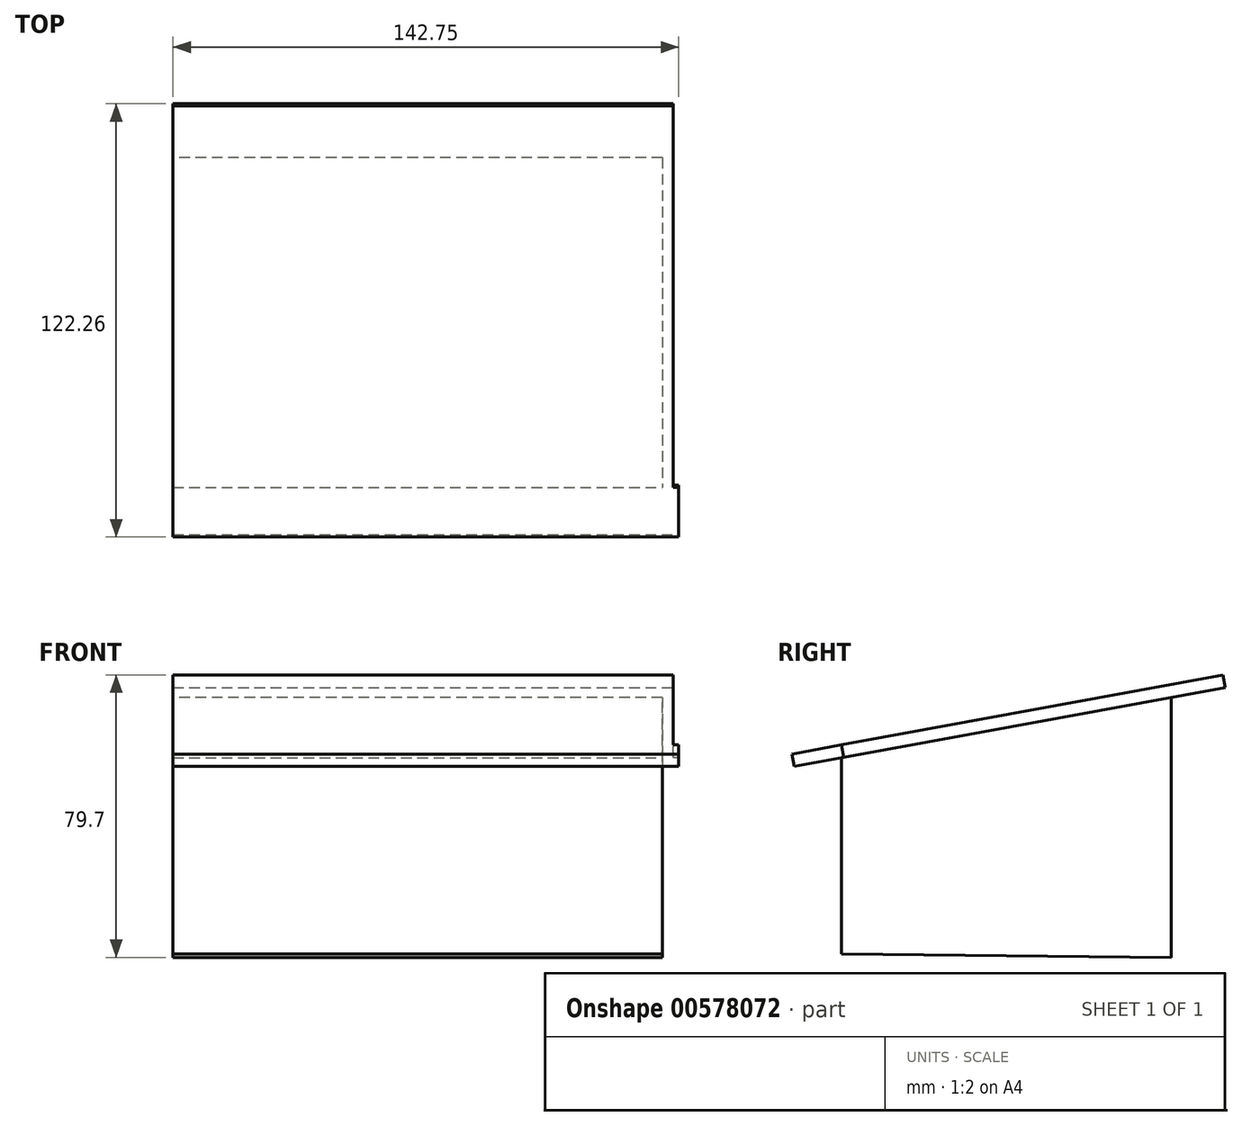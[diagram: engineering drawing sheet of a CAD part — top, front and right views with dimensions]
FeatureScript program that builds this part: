
annotation { "Feature Type Name" : "Feature", "Feature Type Description" : "" }
export const myFeature = defineFeature(function(context is Context, id is Id, definition is map)
    precondition{}
    {
        {
            var Q0;
            Q0=qCreatedBy(makeId("Right.planeOp"),FACE);
            var sketch = newSketch(context, id + "F0", { "sketchPlane" : qUnion([Q0])});
            skLineSegment(sketch, "E0", {"start": v(-41.54, 55.43) * mm, "end": v(-41.54, -3.51) * mm});
            skLineSegment(sketch, "E1", {"start": v(51.47, -4.53) * mm, "end": v(-41.54, -3.51) * mm});
            skLineSegment(sketch, "E2", {"start": v(66.08, 75.17) * mm, "end": v(-41.54, 55.43) * mm});
            skLineSegment(sketch, "E3", {"start": v(-41.54, 55.43) * mm, "end": v(-55.54, 52.86) * mm});
            skLineSegment(sketch, "E4", {"start": v(51.47, -4.53) * mm, "end": v(51.47, 72.5) * mm});
            skSolve(sketch);
        }
        {
            var Q0;
            Q0 = qSketchRegion(id + "F0", true);
            extrude(context, id + "F1", {"entities" : qUnion([Q0]), "depth" : 138.18 * mm, "offsetDistance" : 25.4 * mm});
        }
        {
            var Q0;
            Q0=sQuery(id+"F0.wireOp",EDGE,"E3");
            extrude(context, id + "F2", {"bodyType" : ToolBodyType.SURFACE, "surfaceEntities" : qUnion([Q0]), "depth" : 142.75 * mm, "offsetDistance" : 25.4 * mm});
        }
        {
            var Q0;
            Q0=makeQuery(id+"F2.opExtrude","SWEPT_FACE",FACE,{"disambiguationData":[OSD([sQuery(id+"F0.wireOp",EDGE,"E3")])]});
            extrude(context, id + "F3", {"entities" : qUnion([Q0]), "operationType" : NewBodyOperationType.ADD, "oppositeDirection" : true, "depth" : 3.56 * mm, "offsetDistance" : 25.4 * mm});
        }
        {
            var Q0;
            Q0=sQuery(id+"F0.wireOp",EDGE,"E2");
            extrude(context, id + "F4", {"bodyType" : ToolBodyType.SURFACE, "surfaceEntities" : qUnion([Q0]), "depth" : 141.22 * mm, "offsetDistance" : 25.4 * mm});
        }
        {
            var Q0;
            Q0=makeQuery(id+"F4.opExtrude","SWEPT_FACE",FACE,{"disambiguationData":[OSD([sQuery(id+"F0.wireOp",EDGE,"E2")])]});
            extrude(context, id + "F5", {"entities" : qUnion([Q0]), "operationType" : NewBodyOperationType.ADD, "oppositeDirection" : true, "depth" : 3.56 * mm, "offsetDistance" : 25.4 * mm});
        }
    });
